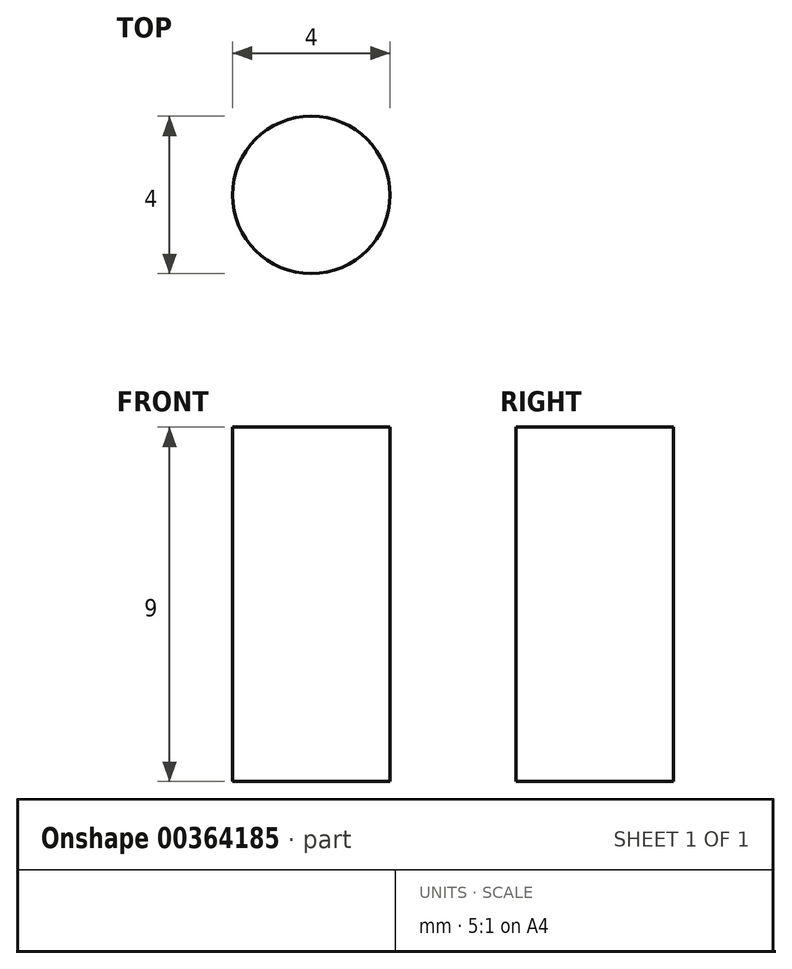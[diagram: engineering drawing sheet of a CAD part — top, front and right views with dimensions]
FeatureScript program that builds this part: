
annotation { "Feature Type Name" : "Feature", "Feature Type Description" : "" }
export const myFeature = defineFeature(function(context is Context, id is Id, definition is map)
    precondition{}
    {
        {
            var Q0;
            Q0=qCreatedBy(makeId("Top.planeOp"),FACE);
            var sketch = newSketch(context, id + "F0", { "sketchPlane" : qUnion([Q0])});
            skCircle(sketch, "E0", {"center": v(0, 0) * mm, "radius": 2 * mm});
            skSolve(sketch);
        }
        {
            var Q0;
            Q0 = qSketchRegion(id + "F0", true);
            extrude(context, id + "F1", {"entities" : qUnion([Q0]), "depth" : 9 * mm});
        }
    });
